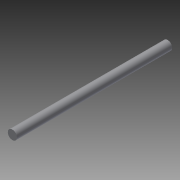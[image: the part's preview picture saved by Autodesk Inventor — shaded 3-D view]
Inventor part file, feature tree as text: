
AUTODESK INVENTOR PART (.ipt)
format: ipt  version: 2014 (Build 180170000, 170)  size: 67,584 bytes
history: native  units: mm
features: extrude x1, sketch x1
ambient origin geometry x8: Origin, YZ Plane, XZ Plane, XY Plane, X Axis, Y Axis, Z Axis, Center Point
bodies: Solid1 (feature_tree)
feature tree (2):
  extrude  "Extrusion1"  Depth=170.0mm TaperAngle=0.0deg
  sketch  "Sketch1"  dims[d0=10.0mm d1=170.0mm d2=0.0mm]
